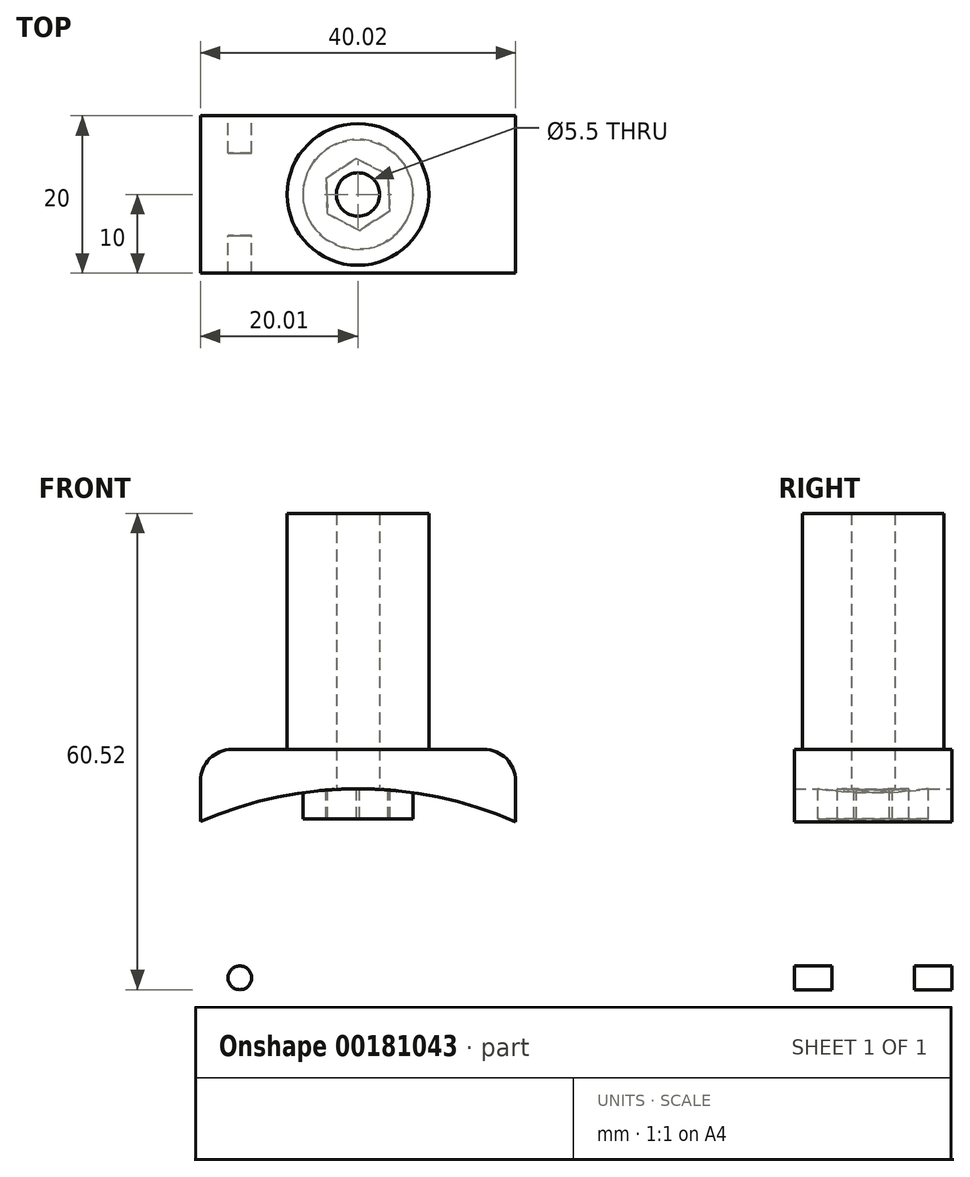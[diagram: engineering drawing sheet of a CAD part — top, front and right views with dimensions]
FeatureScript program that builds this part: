
annotation { "Feature Type Name" : "Feature", "Feature Type Description" : "" }
export const myFeature = defineFeature(function(context is Context, id is Id, definition is map)
    precondition{}
    {
        {
            var Q0;
            Q0=qCreatedBy(makeId("Front.planeOp"),FACE);
            var sketch = newSketch(context, id + "F0", { "sketchPlane" : qUnion([Q0])});
            skCircle(sketch, "E0", {"center": v(-15, -29.5) * mm, "radius": 1.5 * mm});
            skCircle(sketch, "E1", {"center": v(15, -29.5) * mm, "radius": 1.5 * mm});
            skCircle(sketch, "E2", {"center": v(7.76, -26.5) * mm, "radius": 1.5 * mm});
            skCircle(sketch, "E3", {"center": v(0, -25.48) * mm, "radius": 1.5 * mm});
            skCircle(sketch, "E4", {"center": v(-7.77, -26.5) * mm, "radius": 1.5 * mm});
            skLineSegment(sketch, "E5", {"start": v(-10, 34.52) * mm, "end": v(10, 34.52) * mm});
            skLineSegment(sketch, "E6", {"start": v(-16, -0.48) * mm, "end": v(16, -0.48) * mm});
            skLineSegment(sketch, "E7", {"start": v(10, 34.52) * mm, "end": v(10, -0.48) * mm});
            skLineSegment(sketch, "E8", {"start": v(-10, 34.52) * mm, "end": v(-10, -0.48) * mm});
            skLineSegment(sketch, "E9", {"start": v(-20, -29.5) * mm, "end": v(-20, -4.48) * mm});
            skLineSegment(sketch, "E10", {"start": v(20, -29.5) * mm, "end": v(20, -4.48) * mm});
            skArc(sketch, "E11", {"start": v(-20, -29.5) * mm, "mid": v(-17.51, -33.83) * mm, "end": v(-12.5, -33.83) * mm});
            skArc(sketch, "E12", {"start": v(12.16, -33.64) * mm, "mid": v(17.33, -33.94) * mm, "end": v(20, -29.5) * mm});
            skArc(sketch, "E13", {"start": v(12.82, -34.03) * mm, "mid": v(0.18, -30.48) * mm, "end": v(-12.5, -33.83) * mm});
            skArc(sketch, "E14", {"start": v(20, -9.66) * mm, "mid": v(0, -5.48) * mm, "end": v(-20, -9.66) * mm});
            skArc(sketch, "E15", {"start": v(-16, -0.48) * mm, "mid": v(-18.84, -1.65) * mm, "end": v(-20, -4.48) * mm});
            skArc(sketch, "E16", {"start": v(20, -4.48) * mm, "mid": v(18.84, -1.65) * mm, "end": v(16, -0.48) * mm});
            skLineSegment(sketch, "E17", {"start": v(0, -25.48) * mm, "end": v(0, 34.52) * mm});
            skPoint(sketch, "E17.endSnap0", {"position": v(0, 34.52) * mm});
            skLineSegment(sketch, "E18", {"start": v(0, -5.48) * mm, "end": v(13.36, -5.48) * mm});
            skSolve(sketch);
        }
        {
            var Q0;
            Q0=makeQuery(id+"F0.imprint","IMPRINT",FACE,{"disambiguationData":[TD([[makeQuery(id+"F0.imprint","IMPRINT",EDGE,{"derivedFrom":sQuery(id+"F0.wireOp",EDGE,"E0")}),1.0]])]});
            var Q1;
            {var subQ2=sQuery(id+"F0.wireOp",EDGE,"E14");Q1=makeQuery(id+"F0.imprint","IMPRINT",FACE,{"disambiguationData":[TD([[makeQuery(id+"F0.imprint","IMPRINT",EDGE,{"derivedFrom":subQ2}),-1.0]])]});}
            extrude(context, id + "F1", {"entities" : qUnion([Q0, Q1]), "endBound" : BoundingType.SYMMETRIC, "depth" : 20 * mm});
        }
        {
            var Q0;
            Q0=makeQuery(id+"F0.imprint","IMPRINT",FACE,{"disambiguationData":[TD([[makeQuery(id+"F0.imprint","IMPRINT",EDGE,{"derivedFrom":sQuery(id+"F0.wireOp",EDGE,"E0")}),1.0]])]});
            extrude(context, id + "F2", {"entities" : qUnion([Q0]), "operationType" : NewBodyOperationType.REMOVE, "endBound" : BoundingType.SYMMETRIC, "depth" : 10.5 * mm});
        }
        {
            var Q0;
            Q0=makeQuery(id+"F1.opExtrude","SWEPT_FACE",FACE,{"disambiguationData":[OSD([sQuery(id+"F0.wireOp",EDGE,"E6")])]});
            var sketch = newSketch(context, id + "F3", { "sketchPlane" : qUnion([Q0])});
            skCircle(sketch, "E19", {"center": v(0, 0) * mm, "radius": 9 * mm});
            skCircle(sketch, "E20.cCircle", {"center": v(0, 0) * mm, "radius": 3.95 * mm, "construction": true});
            skLineSegment(sketch, "E20.0", {"start": v(4.05, -2.1) * mm, "end": v(0.2, -4.56) * mm});
            skLineSegment(sketch, "E20.1", {"start": v(0.2, -4.56) * mm, "end": v(-3.84, -2.46) * mm});
            skLineSegment(sketch, "E20.2", {"start": v(-3.84, -2.46) * mm, "end": v(-4.05, 2.1) * mm});
            skLineSegment(sketch, "E20.3", {"start": v(-4.05, 2.1) * mm, "end": v(-0.2, 4.56) * mm});
            skLineSegment(sketch, "E20.4", {"start": v(-0.2, 4.56) * mm, "end": v(3.84, 2.46) * mm});
            skLineSegment(sketch, "E20.5", {"start": v(3.84, 2.46) * mm, "end": v(4.05, -2.1) * mm});
            skPoint(sketch, "E20.0.midPoint", {"position": v(2.13, -3.33) * mm});
            skCircle(sketch, "E21", {"center": v(0, 0) * mm, "radius": 7 * mm});
            skCircle(sketch, "E22", {"center": v(0, 0) * mm, "radius": 2.75 * mm});
            skSolve(sketch);
        }
        {
            var Q0;
            Q0=makeQuery(id+"F3.imprint","IMPRINT",FACE,{"disambiguationData":[TD([[makeQuery(id+"F3.imprint","IMPRINT",EDGE,{"derivedFrom":sQuery(id+"F3.wireOp",EDGE,"E19")}),1.0]])]});
            var Q1;
            Q1=makeQuery(id+"F3.imprint","IMPRINT",FACE,{"disambiguationData":[TD([[makeQuery(id+"F3.imprint","IMPRINT",EDGE,{"derivedFrom":sQuery(id+"F3.wireOp",EDGE,"E20.0")}),1.0]])]});
            var Q2;
            Q2=makeQuery(id+"F3.imprint","IMPRINT",FACE,{"disambiguationData":[TD([[makeQuery(id+"F3.imprint","IMPRINT",EDGE,{"derivedFrom":sQuery(id+"F3.wireOp",EDGE,"E20.0")}),-1.0]])]});
            extrude(context, id + "F4", {"entities" : qUnion([Q0, Q1, Q2]), "operationType" : NewBodyOperationType.ADD, "depth" : 30 * mm});
        }
        {
            var Q0;
            Q0=makeQuery(id+"F3.imprint","IMPRINT",FACE,{"disambiguationData":[TD([[makeQuery(id+"F3.imprint","IMPRINT",EDGE,{"derivedFrom":sQuery(id+"F3.wireOp",EDGE,"E20.0")}),1.0]])]});
            extrude(context, id + "F5", {"entities" : qUnion([Q0]), "operationType" : NewBodyOperationType.ADD, "oppositeDirection" : true, "depth" : 8.8 * mm});
        }
        {
            var Q0;
            Q0=makeQuery(id+"F3.imprint","IMPRINT",FACE,{"disambiguationData":[TD([[makeQuery(id+"F3.imprint","IMPRINT",EDGE,{"derivedFrom":sQuery(id+"F3.wireOp",EDGE,"E22")}),1.0]])]});
            extrude(context, id + "F6", {"entities" : qUnion([Q0]), "operationType" : NewBodyOperationType.REMOVE, "endBound" : BoundingType.UP_TO_NEXT, "oppositeDirection" : true, "depth" : 25 * mm});
        }
    });
